# Revit family: 1303a_omni_ir
name_source: partatom
category: Communication Devices
units: mm (PartAtom-declared; Revit-internal decimal feet)

## family parameters
Cut with Voids When Loaded = No
Host = Face
Maintain Annotation Orientation = No
OmniClass Number = 23.85.80.11.27
OmniClass Title = Lighting Controls
Part Type = Normal
Room Calculation Point = No
Round Connector Dimension = Use Diameter
Shared = Yes

## types (1)
- 1303a_omni_ir
    Assembly Code = D5090
    Certifications = UL and cUL listed
    Coverage = 450- 1500 sq ft, based on model
    Default Elevation = 48 "
    Description = The OMNI DT combines ultrasonic (US) and passive infrared (PIR) technologies
to turn lighting on and off based on occupancy. This dual technology provides
accurate turn-ons while virtually eliminating false-offs. This sensor features
Controls' patented IntelliDAPT® technology, which makes all the sensor
adjustments automatically
    Features = IntelliDAPT self-adaptive technology—no manual adjustment required 
 All-digital passive infrared (PIR) sensor 
Non-volatile memory for sensor settings 
 450 - 1,500 square-foot coverage area (depending on model) 
 Optional relay and photocell control 
 Optional Quick to Install (QTI) connector 
UL and cUL listed 
California Title 24 compliant
Five-year limited warranty
 Low voltage device: 24 Vdc
    Housing Material = Paint -  Matte White
    Manufacturer = NX Lighting Controls
    Model = OMNI®
 Low Voltage Passive Infrared Ceiling Sensor
    Sensing Element = Paint -  Matte White
    Type Comments = CEILING MOUNT OCCUPANCY SENSORS
    URL = https://www.currentlighting.com
    Warranty = 5-Years Warranty
    Width = 4.5 "

## geometry (parser evidence)
native form markers: Sweep x3
no freeform markers — native parametric forms only
